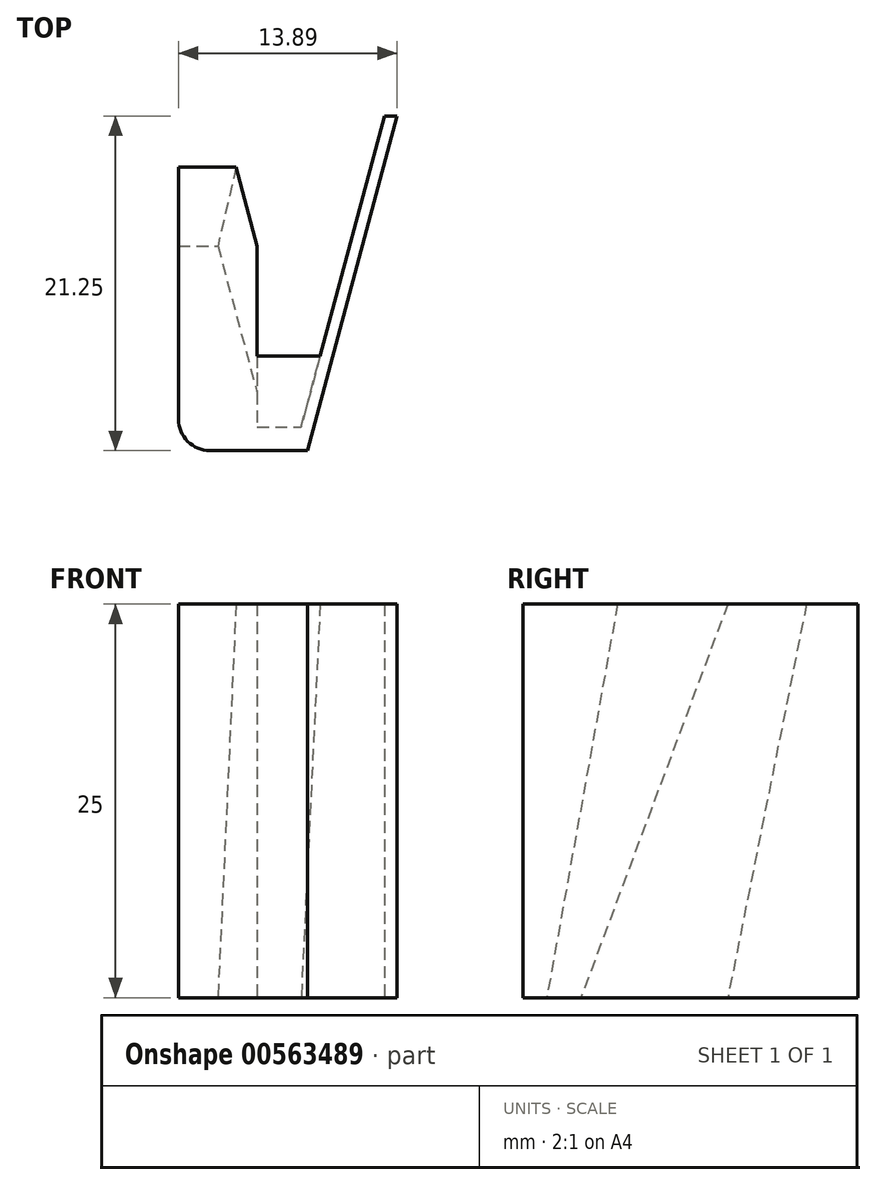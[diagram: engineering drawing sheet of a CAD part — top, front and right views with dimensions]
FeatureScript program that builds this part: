
annotation { "Feature Type Name" : "Feature", "Feature Type Description" : "" }
export const myFeature = defineFeature(function(context is Context, id is Id, definition is map)
    precondition{}
    {
        {
            var Q0;
            Q0=qCreatedBy(makeId("Top.planeOp"),FACE);
            var sketch = newSketch(context, id + "F0", { "sketchPlane" : qUnion([Q0])});
            skLineSegment(sketch, "E0", {"start": v(0, 0) * mm, "end": v(0, 18) * mm});
            skLineSegment(sketch, "E1", {"start": v(0, 18) * mm, "end": v(3.66, 18) * mm});
            skLineSegment(sketch, "E2", {"start": v(5, 6) * mm, "end": v(9, 6) * mm});
            skLineSegment(sketch, "E3", {"start": v(13.09, 21.25) * mm, "end": v(13.89, 21.25) * mm});
            skLineSegment(sketch, "E4", {"start": v(13.89, 21.25) * mm, "end": v(8.2, 0) * mm});
            skLineSegment(sketch, "E5", {"start": v(8.2, 0) * mm, "end": v(0, 0) * mm});
            skLineSegment(sketch, "E6", {"start": v(3.66, 18) * mm, "end": v(5, 13) * mm});
            skLineSegment(sketch, "E7", {"start": v(5, 13) * mm, "end": v(5, 6) * mm});
            skLineSegment(sketch, "E8", {"start": v(13.09, 21.25) * mm, "end": v(9, 6) * mm});
            skSolve(sketch);
        }
        {
            var Q0;
            Q0=qCreatedBy(makeId("Top.planeOp"),FACE);
            cPlane(context, id + "F1", {"entities" : qUnion([Q0]), "cplaneType" : CPlaneType.OFFSET, "offset" : 25 * mm, "oppositeDirection" : true, "width" : 150 * mm, "height" : 150 * mm});
        }
        {
            var Q0;
            Q0=qCreatedBy(id+"F1.planeOp",FACE);
            var sketch = newSketch(context, id + "F2", { "sketchPlane" : qUnion([Q0])});
            skLineSegment(sketch, "E9", {"start": v(0, 0) * mm, "end": v(0, 13) * mm});
            skLineSegment(sketch, "E10", {"start": v(0, 13) * mm, "end": v(2.5, 13) * mm});
            skLineSegment(sketch, "E11", {"start": v(2.5, 13) * mm, "end": v(5, 3.67) * mm});
            skLineSegment(sketch, "E12", {"start": v(5, 3.67) * mm, "end": v(5, 1.5) * mm});
            skLineSegment(sketch, "E13", {"start": v(5, 1.5) * mm, "end": v(7.8, 1.5) * mm});
            skLineSegment(sketch, "E14", {"start": v(7.8, 1.5) * mm, "end": v(13.09, 21.25) * mm});
            skLineSegment(sketch, "E15", {"start": v(13.09, 21.25) * mm, "end": v(13.89, 21.25) * mm});
            skLineSegment(sketch, "E16", {"start": v(13.89, 21.25) * mm, "end": v(8.2, 0) * mm});
            skLineSegment(sketch, "E17", {"start": v(8.2, 0) * mm, "end": v(0, 0) * mm});
            skSolve(sketch);
        }
        {
            var Q0;
            Q0=makeQuery(id+"F0.imprint","IMPRINT",FACE,{"disambiguationData":[TD([[makeQuery(id+"F0.imprint","IMPRINT",EDGE,{"derivedFrom":sQuery(id+"F0.wireOp",EDGE,"E0")}),-1.0]])]});
            var Q1;
            Q1=makeQuery(id+"F2.imprint","IMPRINT",FACE,{"disambiguationData":[TD([[makeQuery(id+"F2.imprint","IMPRINT",EDGE,{"derivedFrom":sQuery(id+"F2.wireOp",EDGE,"E9")}),-1.0]])]});
            loft(context, id + "F3", {"sheetProfilesArray" : [{ "sheetProfileEntities" : qUnion([Q0]) }, { "sheetProfileEntities" : qUnion([Q1]) }]});
        }
        {
            var Q0;
            Q0=makeQuery(id+"F3.opLoft","SWEPT_EDGE",EDGE,{"disambiguationData":[OSD([sQuery(id+"F0.wireOp",EDGE,"E0"),sQuery(id+"F0.wireOp",EDGE,"E5"),sQuery(id+"F2.wireOp",EDGE,"E9"),sQuery(id+"F2.wireOp",EDGE,"E17")])]});
            fillet(context, id + "F4", {"entities" : qUnion([Q0]), "radius" : 2 * mm, "tangentPropagation" : true, "allowEdgeOverflow" : false});
        }
    });
